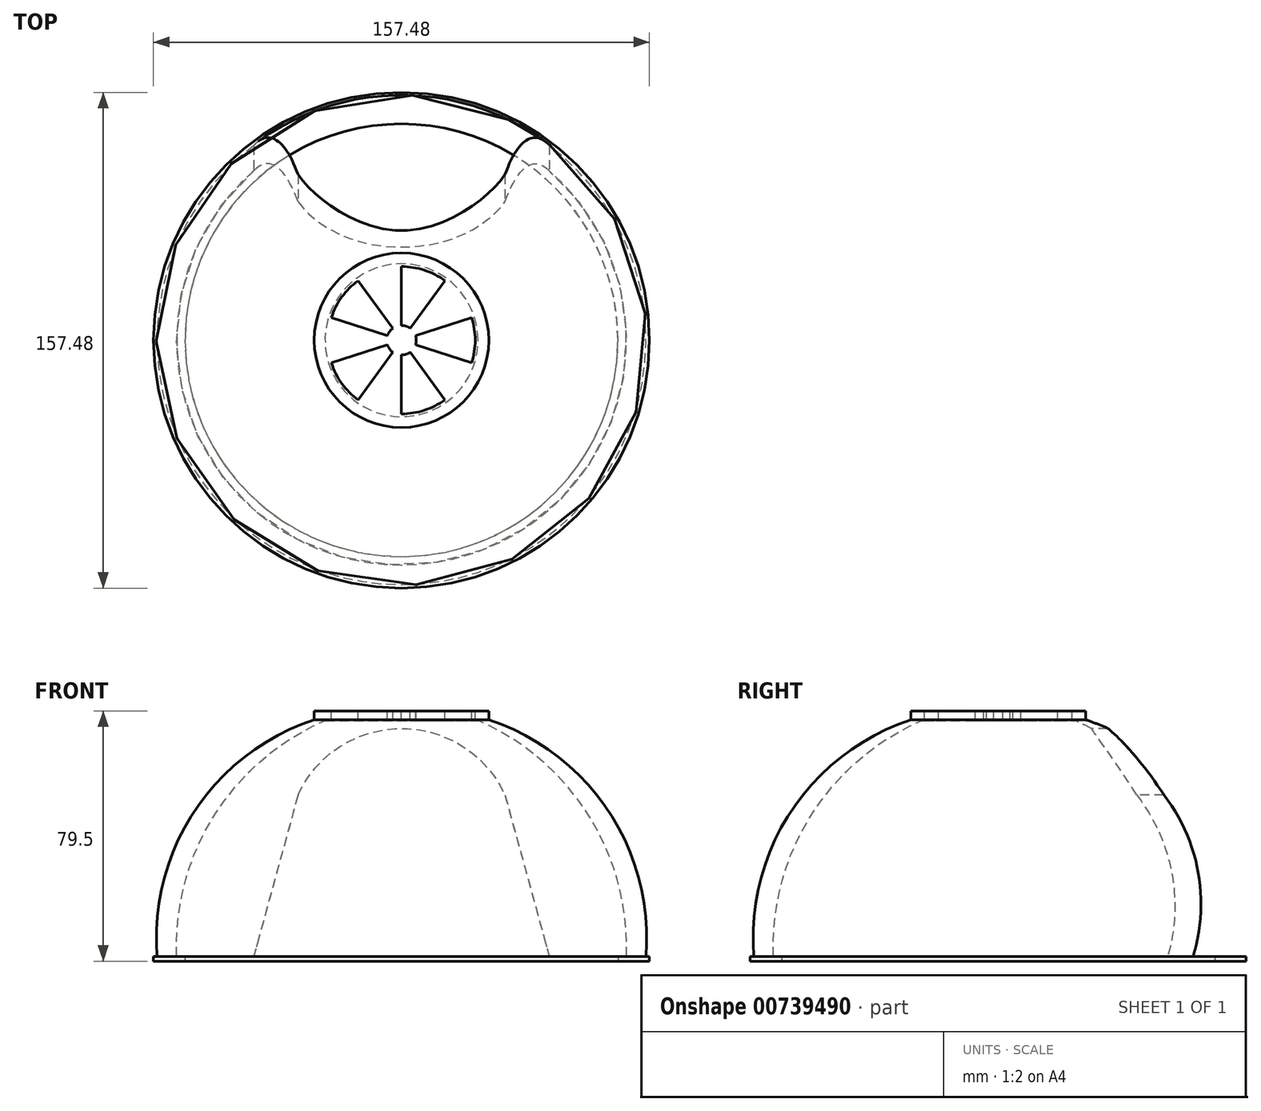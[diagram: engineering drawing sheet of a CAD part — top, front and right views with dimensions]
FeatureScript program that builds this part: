
annotation { "Feature Type Name" : "Feature", "Feature Type Description" : "" }
export const myFeature = defineFeature(function(context is Context, id is Id, definition is map)
    precondition{}
    {
        {
            var Q0;
            Q0=qCreatedBy(makeId("Top.planeOp"),FACE);
            var sketch = newSketch(context, id + "F0", { "sketchPlane" : qUnion([Q0])});
            skCircle(sketch, "E0", {"center": v(0, 0) * mm, "radius": 78.74 * mm});
            skSolve(sketch);
        }
        {
            var Q0;
            Q0 = qSketchRegion(id + "F0", true);
            extrude(context, id + "F1", {"entities" : qUnion([Q0]), "depth" : 1.52 * mm, "offsetDistance" : 25.4 * mm});
        }
        {
            var Q0;
            Q0=qCreatedBy(makeId("Top.planeOp"),FACE);
            var sketch = newSketch(context, id + "F2", { "sketchPlane" : qUnion([Q0])});
            skCircle(sketch, "E1", {"center": v(0, 0) * mm, "radius": 27.72 * mm});
            skSolve(sketch);
        }
        {
            var Q0;
            Q0 = qSketchRegion(id + "F2", true);
            extrude(context, id + "F3", {"entities" : qUnion([Q0]), "depth" : 79.5 * mm, "offsetDistance" : 25.4 * mm, "hasSecondDirection" : true, "secondDirectionOppositeDirection" : false, "secondDirectionDepth" : 76.45 * mm});
        }
        {
            var Q0;
            Q0=qCreatedBy(makeId("Front.planeOp"),FACE);
            var sketch = newSketch(context, id + "F4", { "sketchPlane" : qUnion([Q0])});
            skLineSegment(sketch, "E2", {"start": v(0, 75.33) * mm, "end": v(0, -15.33) * mm});
            skLineSegment(sketch, "E3", {"start": v(-77.48, 0) * mm, "end": v(-71.3, 0) * mm});
            skArc(sketch, "E4", {"start": v(-25.88, 77.26) * mm, "mid": v(-65.57, 47.9) * mm, "end": v(-77.48, 0) * mm});
            skArc(sketch, "E5", {"start": v(-22.34, 77.26) * mm, "mid": v(-59.3, 46.53) * mm, "end": v(-71.3, 0) * mm});
            skLineSegment(sketch, "E6", {"start": v(-25.88, 77.26) * mm, "end": v(-22.34, 77.26) * mm});
            skSolve(sketch);
        }
        {
            var Q0;
            Q0=makeQuery(id+"F4.imprint","IMPRINT",FACE,{"disambiguationData":[TD([[makeQuery(id+"F4.imprint","IMPRINT",EDGE,{"derivedFrom":sQuery(id+"F4.wireOp",EDGE,"E3")}),1.0]])]});
            var Q1;
            Q1=sQuery(id+"F4.wireOp",EDGE,"E2");
            revolve(context, id + "F5", {"operationType" : NewBodyOperationType.ADD, "surfaceOperationType" : NewSurfaceOperationType.NEW, "entities" : qUnion([Q0]), "axis" : qUnion([Q1]), "revolveType" : RevolveType.FULL});
        }
        {
            var Q0;
            Q0=qCreatedBy(makeId("Top.planeOp"),FACE);
            var sketch = newSketch(context, id + "F6", { "sketchPlane" : qUnion([Q0])});
            skCircle(sketch, "E7", {"center": v(0, 0) * mm, "radius": 68.74 * mm});
            skSolve(sketch);
        }
        {
            var Q0;
            Q0 = qSketchRegion(id + "F6", true);
            extrude(context, id + "F7", {"entities" : qUnion([Q0]), "operationType" : NewBodyOperationType.REMOVE, "depth" : 18.54 * mm, "offsetDistance" : 25.4 * mm});
        }
        {
            var Q0;
            Q0=qCreatedBy(makeId("Front.planeOp"),FACE);
            var sketch = newSketch(context, id + "F8", { "sketchPlane" : qUnion([Q0])});
            skLineSegment(sketch, "E8", {"start": v(-46.9, 1.52) * mm, "end": v(46.9, 1.52) * mm});
            skLineSegment(sketch, "E9", {"start": v(0, 65.26) * mm, "end": v(0, -14.16) * mm});
            skPoint(sketch, "E10", {"position": v(0, 1.52) * mm});
            skLineSegment(sketch, "E11", {"start": v(-46.9, 1.52) * mm, "end": v(-32.87, 52.79) * mm});
            skLineSegment(sketch, "E12.MirrorCS", {"start": v(46.9, 1.52) * mm, "end": v(32.87, 52.79) * mm});
            skArc(sketch, "E13", {"start": v(32.87, 52.79) * mm, "mid": v(0, 73.92) * mm, "end": v(-32.87, 52.79) * mm});
            skSolve(sketch);
        }
        {
            var Q0;
            Q0 = qSketchRegion(id + "F8", true);
            extrude(context, id + "F9", {"entities" : qUnion([Q0]), "operationType" : NewBodyOperationType.REMOVE, "oppositeDirection" : true, "depth" : 87.38 * mm, "offsetDistance" : 25.4 * mm});
        }
        {
            var Q0;
            Q0=qCreatedBy(makeId("Front.planeOp"),FACE);
            var sketch = newSketch(context, id + "F10", { "sketchPlane" : qUnion([Q0])});
            skLineSegment(sketch, "E14", {"start": v(0, -12.27) * mm, "end": v(0, 89.61) * mm});
            skSolve(sketch);
        }
        {
            var Q0;
            Q0=makeQuery(id+"F3.opExtrude","CAP_FACE",FACE,{"disambiguationData":[OSD([sQuery(id+"F2.wireOp",EDGE,"E1")])],"isStart":false});
            var sketch = newSketch(context, id + "F11", { "sketchPlane" : qUnion([Q0])});
            skLineSegment(sketch, "E15", {"start": v(0, 4.68) * mm, "end": v(0, 23.4) * mm});
            skLineSegment(sketch, "E16.1.0", {"start": v(-2.75, 3.78) * mm, "end": v(-13.75, 18.92) * mm});
            skLineSegment(sketch, "E16.2.0", {"start": v(-4.45, 1.45) * mm, "end": v(-22.25, 7.23) * mm});
            skLineSegment(sketch, "E16.3.0", {"start": v(-4.45, -1.45) * mm, "end": v(-22.25, -7.23) * mm});
            skLineSegment(sketch, "E16.4.0", {"start": v(-2.75, -3.78) * mm, "end": v(-13.75, -18.92) * mm});
            skLineSegment(sketch, "E16.5.0", {"start": v(0, -4.68) * mm, "end": v(0, -23.4) * mm});
            skLineSegment(sketch, "E16.6.0", {"start": v(2.75, -3.78) * mm, "end": v(13.75, -18.92) * mm});
            skLineSegment(sketch, "E16.7.0", {"start": v(4.45, -1.45) * mm, "end": v(22.25, -7.23) * mm});
            skLineSegment(sketch, "E16.8.0", {"start": v(4.45, 1.45) * mm, "end": v(22.25, 7.23) * mm});
            skLineSegment(sketch, "E16.9.0", {"start": v(2.75, 3.78) * mm, "end": v(13.75, 18.92) * mm});
            skPoint(sketch, "E16.center", {"position": v(0, 0) * mm});
            skArc(sketch, "E17", {"start": v(-2.75, 3.78) * mm, "mid": v(-3.78, 2.75) * mm, "end": v(-4.45, 1.45) * mm});
            skArc(sketch, "E18", {"start": v(-13.75, 18.92) * mm, "mid": v(-18.92, 13.75) * mm, "end": v(-22.25, 7.23) * mm});
            skArc(sketch, "E19.trimOffspring", {"start": v(2.75, 3.78) * mm, "mid": v(1.45, 4.45) * mm, "end": v(0, 4.68) * mm});
            skArc(sketch, "E20.trimOffspring", {"start": v(4.45, -1.45) * mm, "mid": v(4.68, 0) * mm, "end": v(4.45, 1.45) * mm});
            skArc(sketch, "E21.trimOffspring", {"start": v(0, -4.68) * mm, "mid": v(1.45, -4.45) * mm, "end": v(2.75, -3.78) * mm});
            skArc(sketch, "E22.trimOffspring", {"start": v(-4.45, -1.45) * mm, "mid": v(-3.78, -2.75) * mm, "end": v(-2.75, -3.78) * mm});
            skArc(sketch, "E23.trimOffspring", {"start": v(-22.25, -7.23) * mm, "mid": v(-18.92, -13.75) * mm, "end": v(-13.75, -18.92) * mm});
            skArc(sketch, "E24.trimOffspring", {"start": v(0, -23.4) * mm, "mid": v(7.23, -22.25) * mm, "end": v(13.75, -18.92) * mm});
            skArc(sketch, "E25.trimOffspring", {"start": v(22.25, -7.23) * mm, "mid": v(23.4, 0) * mm, "end": v(22.25, 7.23) * mm});
            skArc(sketch, "E26.trimOffspring", {"start": v(13.75, 18.92) * mm, "mid": v(7.23, 22.25) * mm, "end": v(0, 23.4) * mm});
            skSolve(sketch);
        }
        {
            var Q0;
            Q0 = qSketchRegion(id + "F11", true);
            extrude(context, id + "F12", {"entities" : qUnion([Q0]), "operationType" : NewBodyOperationType.REMOVE, "oppositeDirection" : true, "depth" : 25.4 * mm, "offsetDistance" : 25.4 * mm});
        }
    });
